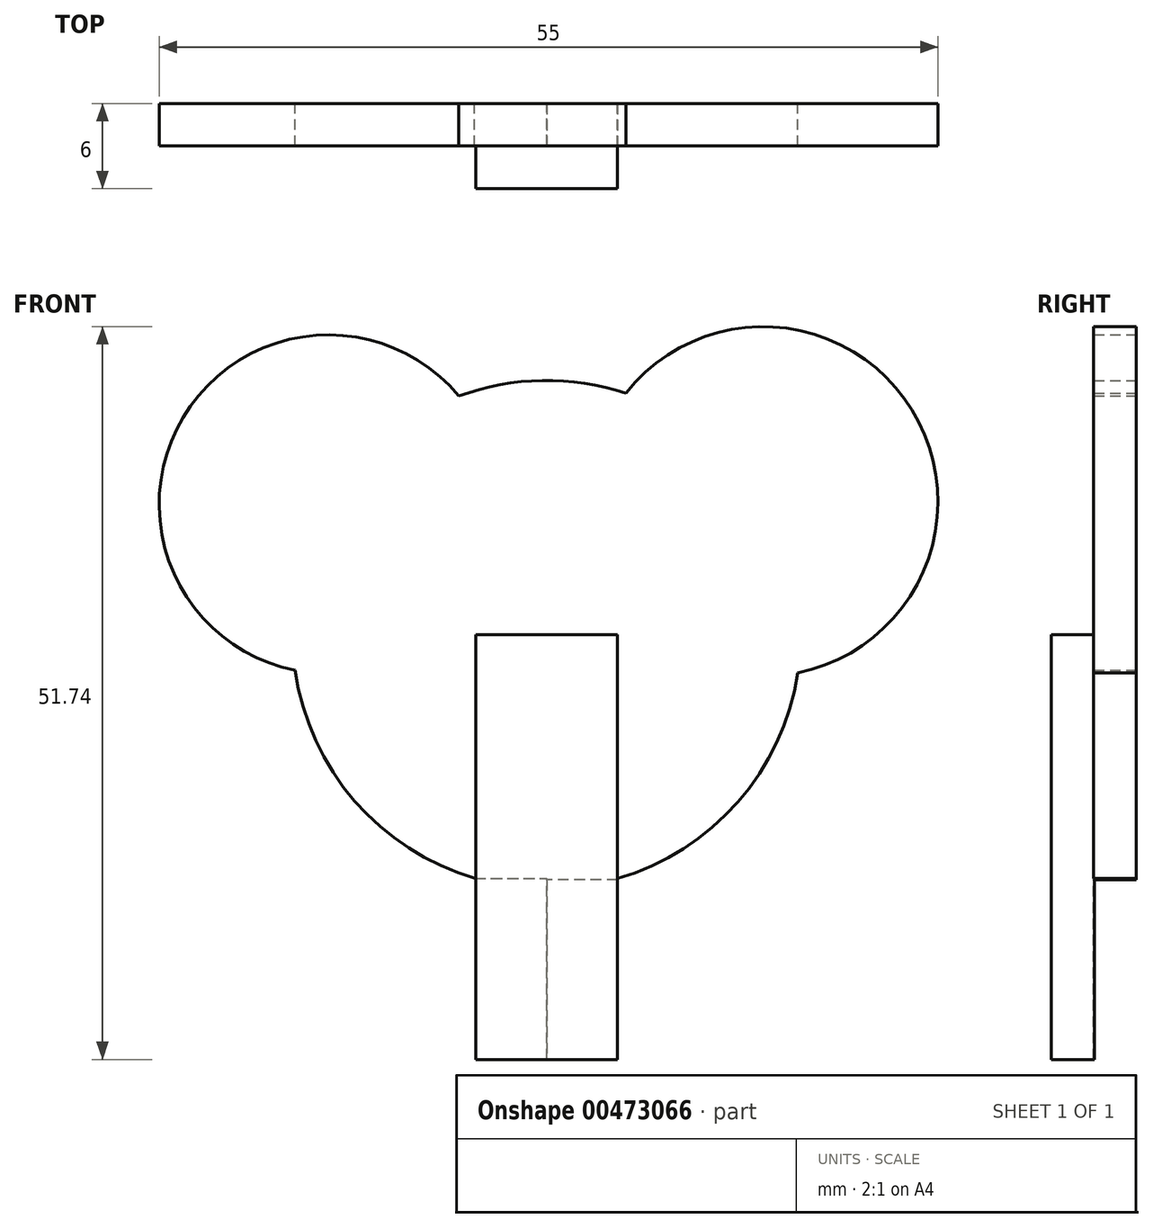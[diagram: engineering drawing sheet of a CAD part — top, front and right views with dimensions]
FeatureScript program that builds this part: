
annotation { "Feature Type Name" : "Feature", "Feature Type Description" : "" }
export const myFeature = defineFeature(function(context is Context, id is Id, definition is map)
    precondition{}
    {
        {
            var Q0;
            Q0=qCreatedBy(makeId("Front.planeOp"),FACE);
            var sketch = newSketch(context, id + "F0", { "sketchPlane" : qUnion([Q0])});
            skArc(sketch, "E0", {"start": v(5.6, 17.05) * mm, "mid": v(-0.32, 17.94) * mm, "end": v(-6.2, 16.84) * mm});
            skArc(sketch, "E1", {"start": v(-6.2, 16.84) * mm, "mid": v(-25.68, 15.33) * mm, "end": v(-17.76, -2.53) * mm});
            skArc(sketch, "E2", {"start": v(17.74, -2.7) * mm, "mid": v(25.8, 15.86) * mm, "end": v(5.6, 17.05) * mm});
            skArc(sketch, "E3.trimOffspring", {"start": v(-17.76, -2.53) * mm, "mid": v(-13.55, -11.76) * mm, "end": v(-5, -17.23) * mm});
            skLineSegment(sketch, "E4.bottom", {"start": v(-5, 0) * mm, "end": v(5, 0) * mm});
            skLineSegment(sketch, "E4.top", {"start": v(-5, -30) * mm, "end": v(5, -30) * mm});
            skLineSegment(sketch, "E4.left", {"start": v(-5, 0) * mm, "end": v(-5, -30) * mm});
            skLineSegment(sketch, "E4.right", {"start": v(5, 0) * mm, "end": v(5, -30) * mm});
            skLineSegment(sketch, "E5", {"start": v(-5, 0) * mm, "end": v(0, 0) * mm});
            skLineSegment(sketch, "E6", {"start": v(0, 0) * mm, "end": v(5, 0) * mm});
            skArc(sketch, "E7.trimOffspring", {"start": v(5, -17.23) * mm, "mid": v(13.5, -11.83) * mm, "end": v(17.74, -2.7) * mm});
            skSolve(sketch);
        }
        {
            var Q0;
            Q0=makeQuery(id+"F0.imprint","IMPRINT",FACE,{"disambiguationData":[TD([[makeQuery(id+"F0.imprint","IMPRINT",EDGE,{"derivedFrom":sQuery(id+"F0.wireOp",EDGE,"E0")}),1.0]])]});
            var Q1;
            {var subQ5=sQuery(id+"F0.wireOp",EDGE,"E4.top");Q1=makeQuery(id+"F0.imprint","IMPRINT",FACE,{"disambiguationData":[TD([[makeQuery(id+"F0.imprint","IMPRINT",EDGE,{"derivedFrom":subQ5}),1.0]])]});}
            extrude(context, id + "F1", {"entities" : qUnion([Q0, Q1]), "depth" : 3 * mm});
        }
        {
            var Q0;
            Q0=makeQuery(id+"F1.opExtrude","CAP_FACE",FACE,{"disambiguationData":[OSD([sQuery(id+"F0.wireOp",EDGE,"E0"),sQuery(id+"F0.wireOp",EDGE,"E1"),sQuery(id+"F0.wireOp",EDGE,"E2"),sQuery(id+"F0.wireOp",EDGE,"E3.trimOffspring"),sQuery(id+"F0.wireOp",EDGE,"E4.top"),sQuery(id+"F0.wireOp",EDGE,"E4.left"),sQuery(id+"F0.wireOp",EDGE,"E4.right"),sQuery(id+"F0.wireOp",EDGE,"E7.trimOffspring")])],"isStart":false});
            var sketch = newSketch(context, id + "F2", { "sketchPlane" : qUnion([Q0])});
            skPoint(sketch, "E8.oppositeSnap0", {"position": v(5, -23.62) * mm});
            skLineSegment(sketch, "E8.bottom", {"start": v(-5, -30) * mm, "end": v(5, -30) * mm});
            skLineSegment(sketch, "E8.top", {"start": v(-5, 0) * mm, "end": v(5, 0) * mm});
            skLineSegment(sketch, "E8.left", {"start": v(-5, -30) * mm, "end": v(-5, 0) * mm});
            skLineSegment(sketch, "E8.right", {"start": v(5, -30) * mm, "end": v(5, 0) * mm});
            skSolve(sketch);
        }
        {
            var Q0;
            {var subQ2=sQuery(id+"F2.wireOp",EDGE,"E8.bottom");Q0=makeQuery(id+"F2.imprint","IMPRINT",FACE,{"disambiguationData":[TD([[makeQuery(id+"F2.imprint","IMPRINT",EDGE,{"derivedFrom":subQ2}),1.0]])]});}
            extrude(context, id + "F3", {"entities" : qUnion([Q0]), "operationType" : NewBodyOperationType.ADD, "depth" : 3 * mm});
        }
        {
            var Q0;
            Q0=qCreatedBy(makeId("Right.planeOp"),FACE);
            var sketch = newSketch(context, id + "F4", { "sketchPlane" : qUnion([Q0])});
            skLineSegment(sketch, "E9.bottom", {"start": v(0, -30.04) * mm, "end": v(-3, -30.04) * mm});
            skLineSegment(sketch, "E9.top", {"start": v(0, -17.2) * mm, "end": v(-3, -17.2) * mm});
            skLineSegment(sketch, "E9.left", {"start": v(0, -30.04) * mm, "end": v(0, -17.2) * mm});
            skLineSegment(sketch, "E9.right", {"start": v(-3, -30.04) * mm, "end": v(-3, -17.2) * mm});
            skSolve(sketch);
        }
        {
            var Q0;
            Q0 = qSketchRegion(id + "F4", true);
            extrude(context, id + "F5", {"entities" : qUnion([Q0]), "operationType" : NewBodyOperationType.REMOVE, "oppositeDirection" : true, "depth" : 10 * mm});
        }
        {
            var Q0;
            Q0=qCreatedBy(makeId("Right.planeOp"),FACE);
            var sketch = newSketch(context, id + "F6", { "sketchPlane" : qUnion([Q0])});
            skLineSegment(sketch, "E10", {"start": v(0, -17.25) * mm, "end": v(0, -29.99) * mm});
            skLineSegment(sketch, "E11.bottom", {"start": v(-2.95, -17.33) * mm, "end": v(-0.05, -17.33) * mm});
            skLineSegment(sketch, "E11.top", {"start": v(-2.95, -30.53) * mm, "end": v(-0.05, -30.53) * mm});
            skLineSegment(sketch, "E11.left", {"start": v(-2.95, -17.33) * mm, "end": v(-2.95, -30.53) * mm});
            skLineSegment(sketch, "E11.right", {"start": v(-0.05, -17.33) * mm, "end": v(-0.05, -30.53) * mm});
            skPoint(sketch, "E11.middle", {"position": v(-1.5, -23.93) * mm});
            skSolve(sketch);
        }
        {
            var Q0;
            Q0 = qSketchRegion(id + "F6", true);
            extrude(context, id + "F7", {"entities" : qUnion([Q0]), "operationType" : NewBodyOperationType.REMOVE, "depth" : 10 * mm});
        }
        {
            var Q0;
            Q0=makeQuery(id+"F7.boolean.opBoolean","COPY",FACE,{"derivedFrom":makeQuery(id+"F7.opExtrude","SWEPT_FACE",FACE,{"disambiguationData":[OSD([sQuery(id+"F6.wireOp",EDGE,"E11.right")])]})});
            extrude(context, id + "F8", {"entities" : qUnion([Q0]), "operationType" : NewBodyOperationType.REMOVE, "oppositeDirection" : true, "depth" : 25 * mm});
        }
    });
